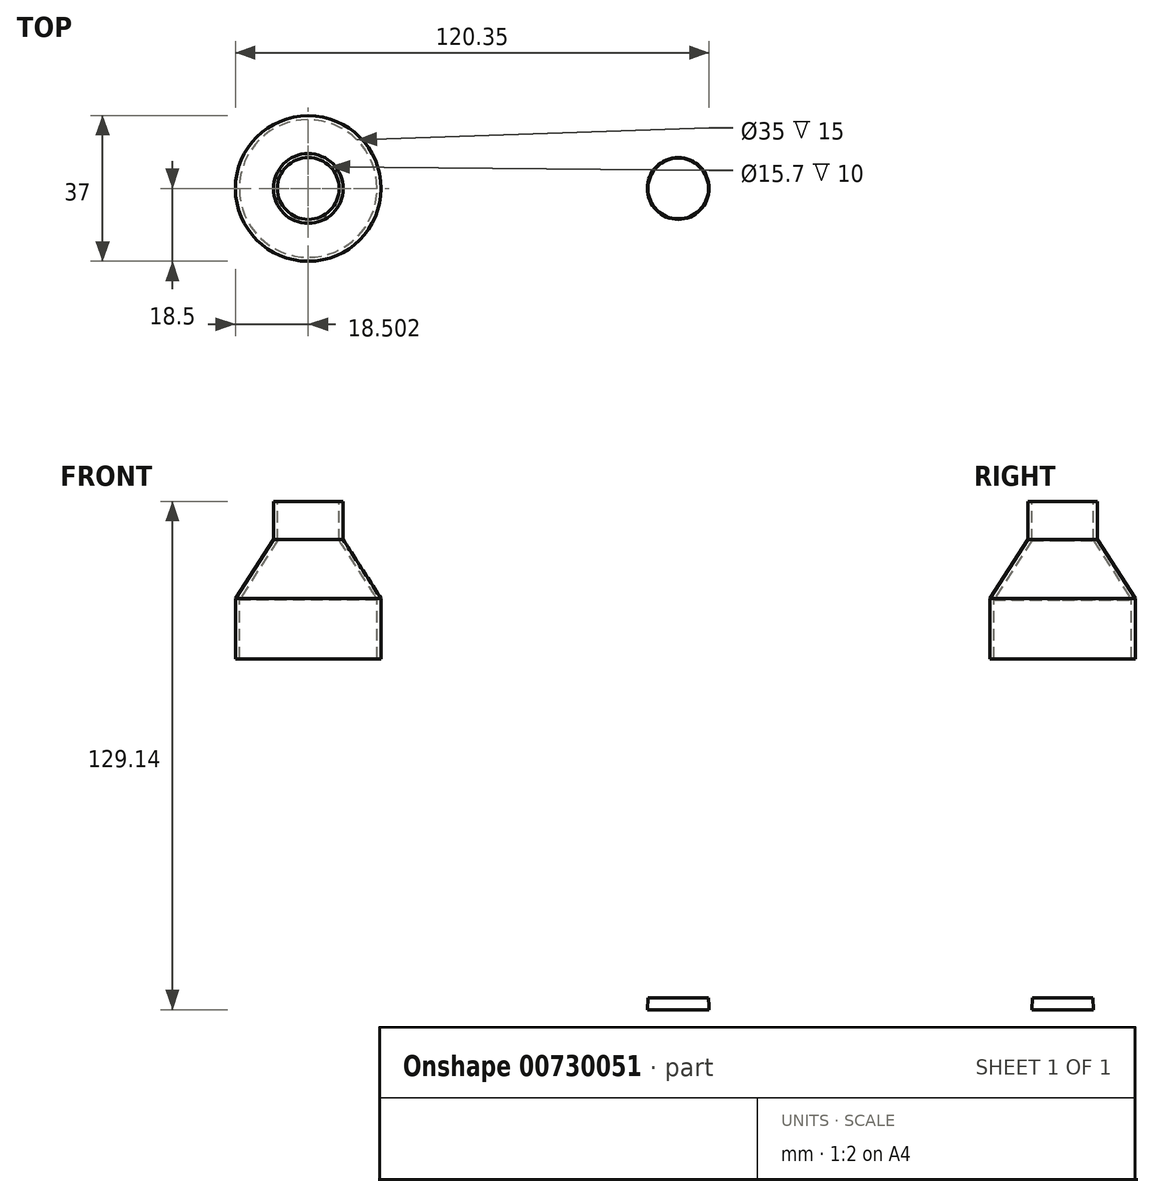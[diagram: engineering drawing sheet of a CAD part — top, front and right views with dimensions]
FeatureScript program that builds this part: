
annotation { "Feature Type Name" : "Feature", "Feature Type Description" : "" }
export const myFeature = defineFeature(function(context is Context, id is Id, definition is map)
    precondition{}
    {
        {
            var Q0;
            Q0=qCreatedBy(makeId("Front.planeOp"),FACE);
            var sketch = newSketch(context, id + "F0", { "sketchPlane" : qUnion([Q0])});
            skLineSegment(sketch, "E0", {"start": v(7.7, 3) * mm, "end": v(7.85, 0) * mm});
            skLineSegment(sketch, "E1", {"start": v(7.7, 3) * mm, "end": v(0, 3) * mm});
            skLineSegment(sketch, "E2", {"start": v(0, 3) * mm, "end": v(0, 0) * mm});
            skLineSegment(sketch, "E3", {"start": v(0, 0) * mm, "end": v(7.85, 0) * mm});
            skLineSegment(sketch, "E4", {"start": v(-101.85, 129.14) * mm, "end": v(-101.85, 119.14) * mm});
            skLineSegment(sketch, "E5", {"start": v(-101.85, 119.14) * mm, "end": v(-111.5, 104.14) * mm});
            skLineSegment(sketch, "E6", {"start": v(-111.5, 104.14) * mm, "end": v(-111.5, 89.14) * mm});
            skLineSegment(sketch, "E7", {"start": v(-94, 141.16) * mm, "end": v(-94, 66.94) * mm, "construction": true});
            skLineSegment(sketch, "E8", {"start": v(-112.5, 89.14) * mm, "end": v(-112.5, 104.44) * mm});
            skLineSegment(sketch, "E9", {"start": v(-112.5, 104.44) * mm, "end": v(-102.85, 119.44) * mm});
            skLineSegment(sketch, "E10", {"start": v(-102.85, 119.44) * mm, "end": v(-102.85, 129.14) * mm});
            skLineSegment(sketch, "E11", {"start": v(-102.85, 129.14) * mm, "end": v(-101.85, 129.14) * mm});
            skLineSegment(sketch, "E12", {"start": v(-112.5, 89.14) * mm, "end": v(-111.5, 89.14) * mm});
            skSolve(sketch);
        }
        {
            var Q0;
            Q0=makeQuery(id+"F0.imprint","IMPRINT",FACE,{"disambiguationData":[TD([[makeQuery(id+"F0.imprint","IMPRINT",EDGE,{"derivedFrom":sQuery(id+"F0.wireOp",EDGE,"E0")}),-1.0]])]});
            var Q1;
            Q1=sQuery(id+"F0.wireOp",EDGE,"E2");
            revolve(context, id + "F1", {"surfaceOperationType" : NewSurfaceOperationType.NEW, "entities" : qUnion([Q0]), "axis" : qUnion([Q1]), "revolveType" : RevolveType.FULL});
        }
        {
            var Q0;
            Q0=makeQuery(id+"F0.imprint","IMPRINT",FACE,{"disambiguationData":[TD([[makeQuery(id+"F0.imprint","IMPRINT",EDGE,{"derivedFrom":sQuery(id+"F0.wireOp",EDGE,"E4")}),-1.0]])]});
            var Q1;
            Q1=sQuery(id+"F0.wireOp",EDGE,"E7");
            revolve(context, id + "F2", {"surfaceOperationType" : NewSurfaceOperationType.NEW, "entities" : qUnion([Q0]), "axis" : qUnion([Q1]), "revolveType" : RevolveType.FULL});
        }
    });
